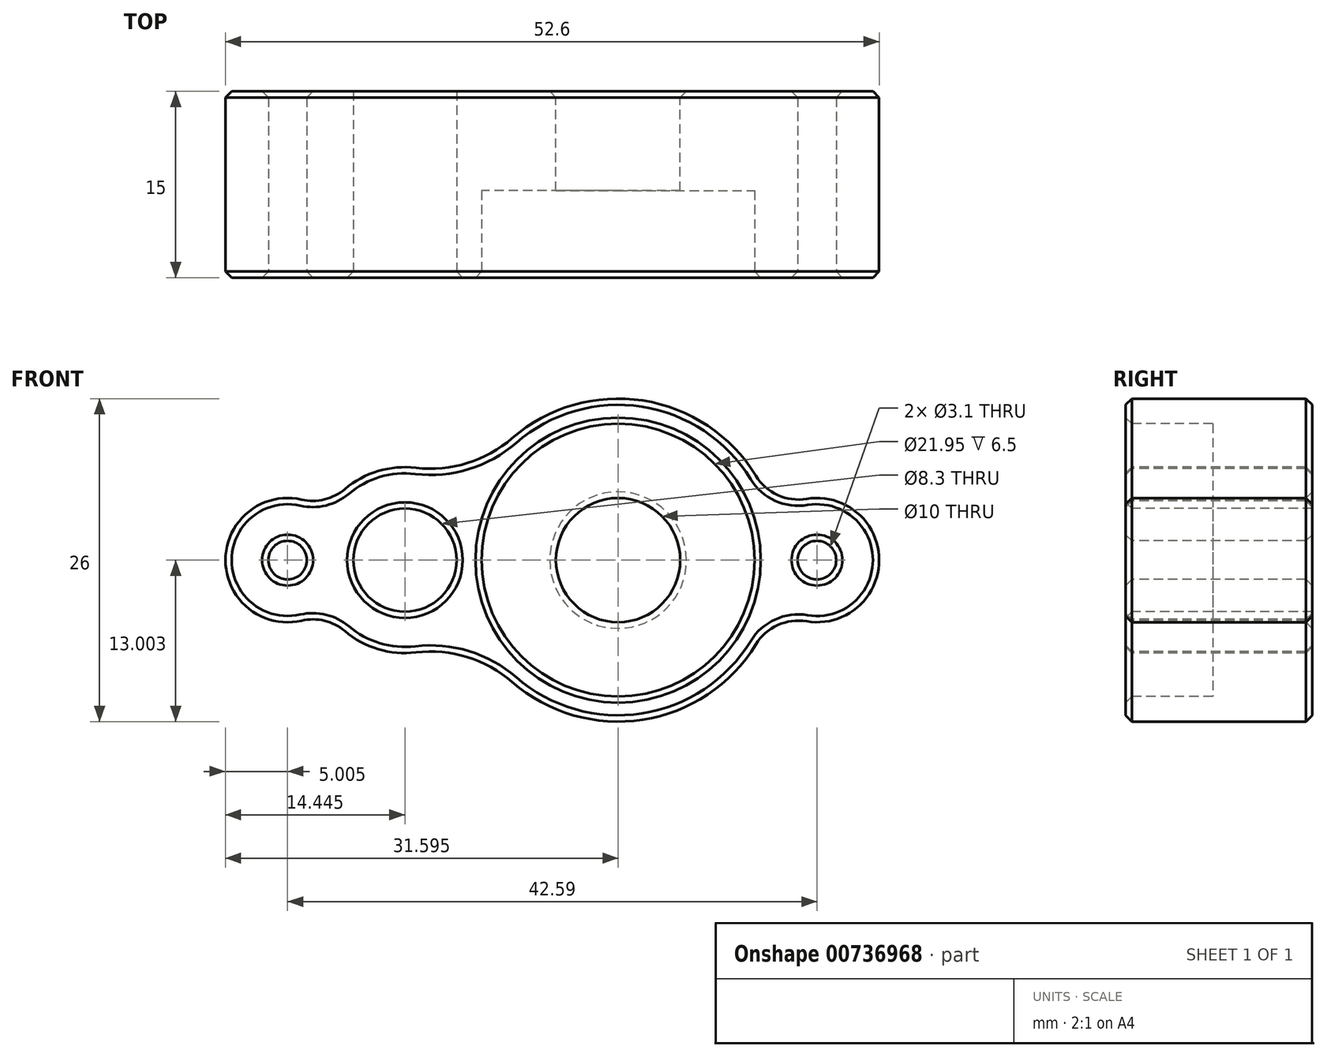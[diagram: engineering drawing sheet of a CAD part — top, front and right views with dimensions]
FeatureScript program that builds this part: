
annotation { "Feature Type Name" : "Feature", "Feature Type Description" : "" }
export const myFeature = defineFeature(function(context is Context, id is Id, definition is map)
    precondition{}
    {
        {
            var Q0;
            Q0=qCreatedBy(makeId("Front.planeOp"),FACE);
            cPlane(context, id + "F0", {"entities" : qUnion([Q0]), "cplaneType" : CPlaneType.OFFSET, "offset" : 7.5 * mm, "width" : 150 * mm, "height" : 150 * mm});
        }
        {
            var Q0;
            Q0=qCreatedBy(id+"F0.planeOp",FACE);
            var sketch = newSketch(context, id + "F1", { "sketchPlane" : qUnion([Q0])});
            skPoint(sketch, "E0.0", {"position": v(-5.85, 0) * mm});
            skPoint(sketch, "E1.0", {"position": v(16.44, 0) * mm});
            skPoint(sketch, "E2.0", {"position": v(-16.04, 0.76) * mm});
            skPoint(sketch, "E3.0", {"position": v(-7.3, 0) * mm});
            skPoint(sketch, "E4.0", {"position": v(19.77, -0.28) * mm});
            skPoint(sketch, "E5.0", {"position": v(22.82, 0.26) * mm});
            skPoint(sketch, "E6.0", {"position": v(-22.82, -0.28) * mm});
            skPoint(sketch, "E7.0", {"position": v(-19.77, 0.26) * mm});
            skPoint(sketch, "E8.0", {"position": v(5.3, 11.14) * mm});
            skPoint(sketch, "E9.0", {"position": v(-11.7, 4.4) * mm});
            skPoint(sketch, "E10.0", {"position": v(-21.03, 1.52) * mm});
            skPoint(sketch, "E11.0", {"position": v(20.3, 1.18) * mm});
            skCircle(sketch, "E12", {"center": v(21.3, 0) * mm, "radius": 1.55 * mm});
            skCircle(sketch, "E13", {"center": v(-21.3, 0) * mm, "radius": 1.55 * mm});
            skPoint(sketch, "E14.0", {"position": v(-22.16, 4.92) * mm});
            skArc(sketch, "E15", {"start": v(-20.17, 4.86) * mm, "mid": v(-26.3, 0) * mm, "end": v(-20.17, -4.88) * mm});
            skPoint(sketch, "E16.0", {"position": v(-12.48, 7.45) * mm});
            skPoint(sketch, "E17.0", {"position": v(4.86, 12.99) * mm});
            skPoint(sketch, "E18.0", {"position": v(22.16, 4.92) * mm});
            skArc(sketch, "E19", {"start": v(-10.97, 7.43) * mm, "mid": v(-14, 7.16) * mm, "end": v(-16.69, 5.7) * mm});
            skArc(sketch, "E20", {"start": v(-3.23, -9.82) * mm, "mid": v(7.28, -12.86) * mm, "end": v(16.38, -6.8) * mm});
            skArc(sketch, "E21.trimOffspring", {"start": v(-16.69, -5.72) * mm, "mid": v(-14, -7.18) * mm, "end": v(-10.97, -7.44) * mm});
            skArc(sketch, "E22.trimOffspring", {"start": v(16.38, 6.78) * mm, "mid": v(7.28, 12.84) * mm, "end": v(-3.23, 9.8) * mm});
            skArc(sketch, "E23.trimOffspring", {"start": v(20.46, -4.94) * mm, "mid": v(26.3, 0) * mm, "end": v(20.46, 4.92) * mm});
            skCircle(sketch, "E24", {"center": v(5.3, 0) * mm, "radius": 10.97 * mm});
            skCircle(sketch, "E25", {"center": v(21.3, 0) * mm, "radius": 1.25 * mm});
            skCircle(sketch, "E26", {"center": v(-21.3, 0) * mm, "radius": 1.25 * mm});
            skPoint(sketch, "E27.visualSharp", {"position": v(-18.22, 3.93) * mm});
            skArc(sketch, "E27.filletArc", {"start": v(-20.17, 4.86) * mm, "mid": v(-18.33, 4.87) * mm, "end": v(-16.69, 5.7) * mm});
            skPoint(sketch, "E28.visualSharp", {"position": v(-18.22, -3.95) * mm});
            skArc(sketch, "E28.filletArc", {"start": v(-16.69, -5.72) * mm, "mid": v(-18.33, -4.89) * mm, "end": v(-20.17, -4.88) * mm});
            skPoint(sketch, "E29.visualSharp", {"position": v(-6.57, 5.3) * mm});
            skArc(sketch, "E29.filletArc", {"start": v(-10.97, 7.43) * mm, "mid": v(-6.85, 7.8) * mm, "end": v(-3.23, 9.8) * mm});
            skPoint(sketch, "E30.visualSharp", {"position": v(-6.57, -5.31) * mm});
            skArc(sketch, "E30.filletArc", {"start": v(-3.23, -9.82) * mm, "mid": v(-6.85, -7.81) * mm, "end": v(-10.97, -7.44) * mm});
            skPoint(sketch, "E31.visualSharp", {"position": v(17.8, -3.58) * mm});
            skArc(sketch, "E31.filletArc", {"start": v(20.46, -4.94) * mm, "mid": v(18.14, -5.24) * mm, "end": v(16.38, -6.8) * mm});
            skPoint(sketch, "E32.visualSharp", {"position": v(17.8, 3.56) * mm});
            skArc(sketch, "E32.filletArc", {"start": v(16.38, 6.78) * mm, "mid": v(18.14, 5.23) * mm, "end": v(20.46, 4.92) * mm});
            skCircle(sketch, "E33", {"center": v(-11.85, 0) * mm, "radius": 4.15 * mm});
            skSolve(sketch);
        }
        {
            var Q0;
            Q0=makeQuery(id+"F1.imprint","IMPRINT",FACE,{"disambiguationData":[TD([[makeQuery(id+"F1.imprint","IMPRINT",EDGE,{"derivedFrom":sQuery(id+"F1.wireOp",EDGE,"ee63c072-4f0e-46bd-9d90-5885ff48c119")}),-1.0]])]});
            var Q1;
            Q1=makeQuery(id+"F1.imprint","IMPRINT",FACE,{"disambiguationData":[TD([[makeQuery(id+"F1.imprint","IMPRINT",EDGE,{"derivedFrom":sQuery(id+"F1.wireOp",EDGE,"E12")}),-1.0]])]});
            extrude(context, id + "F2", {"entities" : qUnion([Q0, Q1]), "oppositeDirection" : true, "depth" : 15 * mm, "offsetDistance" : 25 * mm});
        }
        {
            var Q0;
            Q0=makeQuery(id+"F2.opExtrude","CAP_FACE",FACE,{"disambiguationData":[OSD([sQuery(id+"F1.wireOp",EDGE,"ee63c072-4f0e-46bd-9d90-5885ff48c119"),sQuery(id+"F1.wireOp",EDGE,"E12"),sQuery(id+"F1.wireOp",EDGE,"E13"),sQuery(id+"F1.wireOp",EDGE,"E15"),sQuery(id+"F1.wireOp",EDGE,"E19"),sQuery(id+"F1.wireOp",EDGE,"E20"),sQuery(id+"F1.wireOp",EDGE,"E21.trimOffspring"),sQuery(id+"F1.wireOp",EDGE,"E22.trimOffspring"),sQuery(id+"F1.wireOp",EDGE,"E23.trimOffspring"),sQuery(id+"F1.wireOp",EDGE,"E24"),sQuery(id+"F1.wireOp",EDGE,"E27.filletArc"),sQuery(id+"F1.wireOp",EDGE,"E28.filletArc"),sQuery(id+"F1.wireOp",EDGE,"E29.filletArc"),sQuery(id+"F1.wireOp",EDGE,"E30.filletArc"),sQuery(id+"F1.wireOp",EDGE,"E31.filletArc"),sQuery(id+"F1.wireOp",EDGE,"E32.filletArc")])],"isStart":false});
            var sketch = newSketch(context, id + "F3", { "sketchPlane" : qUnion([Q0])});
            skCircle(sketch, "E34.0", {"center": v(-5.3, 0) * mm, "radius": 10.97 * mm});
            skCircle(sketch, "E35", {"center": v(-5.3, 0) * mm, "radius": 5 * mm});
            skSolve(sketch);
        }
        {
            var Q0;
            Q0=makeQuery(id+"F3.imprint","IMPRINT",FACE,{"disambiguationData":[TD([[makeQuery(id+"F3.imprint","IMPRINT",EDGE,{"derivedFrom":sQuery(id+"F3.wireOp",EDGE,"E34.0")}),-1.0]])]});
            extrude(context, id + "F4", {"entities" : qUnion([Q0]), "operationType" : NewBodyOperationType.ADD, "oppositeDirection" : true, "depth" : 8 * mm, "offsetDistance" : 25 * mm});
        }
        {
            var Q0;
            Q0=makeQuery(id+"F2.opExtrude","CAP_EDGE",EDGE,{"disambiguationData":[OSD([sQuery(id+"F1.wireOp",EDGE,"E29.filletArc")])],"isStart":true});
            var Q1;
            Q1=makeQuery(id+"F2.opExtrude","CAP_EDGE",EDGE,{"disambiguationData":[OSD([sQuery(id+"F1.wireOp",EDGE,"E22.trimOffspring")])],"isStart":true});
            var Q2;
            Q2=makeQuery(id+"F2.opExtrude","CAP_EDGE",EDGE,{"disambiguationData":[OSD([sQuery(id+"F1.wireOp",EDGE,"E32.filletArc")])],"isStart":true});
            var Q3;
            Q3=makeQuery(id+"F2.opExtrude","CAP_EDGE",EDGE,{"disambiguationData":[OSD([sQuery(id+"F1.wireOp",EDGE,"E23.trimOffspring")])],"isStart":true});
            var Q4;
            Q4=makeQuery(id+"F2.opExtrude","CAP_EDGE",EDGE,{"disambiguationData":[OSD([sQuery(id+"F1.wireOp",EDGE,"E31.filletArc")])],"isStart":true});
            var Q5;
            Q5=makeQuery(id+"F2.opExtrude","CAP_EDGE",EDGE,{"disambiguationData":[OSD([sQuery(id+"F1.wireOp",EDGE,"E20")])],"isStart":true});
            var Q6;
            Q6=makeQuery(id+"F2.opExtrude","CAP_EDGE",EDGE,{"disambiguationData":[OSD([sQuery(id+"F1.wireOp",EDGE,"E30.filletArc")])],"isStart":true});
            var Q7;
            Q7=makeQuery(id+"F2.opExtrude","CAP_EDGE",EDGE,{"disambiguationData":[OSD([sQuery(id+"F1.wireOp",EDGE,"E21.trimOffspring")])],"isStart":true});
            var Q8;
            Q8=makeQuery(id+"F2.opExtrude","CAP_EDGE",EDGE,{"disambiguationData":[OSD([sQuery(id+"F1.wireOp",EDGE,"E28.filletArc")])],"isStart":true});
            var Q9;
            Q9=makeQuery(id+"F2.opExtrude","CAP_EDGE",EDGE,{"disambiguationData":[OSD([sQuery(id+"F1.wireOp",EDGE,"E15")])],"isStart":true});
            var Q10;
            Q10=makeQuery(id+"F2.opExtrude","CAP_EDGE",EDGE,{"disambiguationData":[OSD([sQuery(id+"F1.wireOp",EDGE,"E27.filletArc")])],"isStart":true});
            var Q11;
            Q11=makeQuery(id+"F2.opExtrude","CAP_EDGE",EDGE,{"disambiguationData":[OSD([sQuery(id+"F1.wireOp",EDGE,"E19")])],"isStart":true});
            var Q12;
            Q12=makeQuery(id+"F2.opExtrude","CAP_EDGE",EDGE,{"disambiguationData":[OSD([sQuery(id+"F1.wireOp",EDGE,"E24")])],"isStart":true});
            var Q13;
            Q13=makeQuery(id+"F2.opExtrude","CAP_EDGE",EDGE,{"disambiguationData":[OSD([sQuery(id+"F1.wireOp",EDGE,"ee63c072-4f0e-46bd-9d90-5885ff48c119")])],"isStart":true});
            var Q14;
            Q14=makeQuery(id+"F2.opExtrude","CAP_EDGE",EDGE,{"disambiguationData":[OSD([sQuery(id+"F1.wireOp",EDGE,"E13")])],"isStart":true});
            var Q15;
            Q15=makeQuery(id+"F2.opExtrude","CAP_EDGE",EDGE,{"disambiguationData":[OSD([sQuery(id+"F1.wireOp",EDGE,"E12")])],"isStart":true});
            var Q16;
            Q16=makeQuery(id+"F2.opExtrude","CAP_EDGE",EDGE,{"disambiguationData":[OSD([sQuery(id+"F1.wireOp",EDGE,"E22.trimOffspring")])],"isStart":false});
            var Q17;
            Q17=makeQuery(id+"F2.opExtrude","CAP_EDGE",EDGE,{"disambiguationData":[OSD([sQuery(id+"F1.wireOp",EDGE,"ee63c072-4f0e-46bd-9d90-5885ff48c119")])],"isStart":false});
            var Q18;
            Q18=makeQuery(id+"F2.opExtrude","CAP_EDGE",EDGE,{"disambiguationData":[OSD([sQuery(id+"F1.wireOp",EDGE,"E13")])],"isStart":false});
            var Q19;
            Q19=makeQuery(id+"F4.opExtrude","CAP_EDGE",EDGE,{"disambiguationData":[OSD([sQuery(id+"F3.wireOp",EDGE,"E35")])],"isStart":true});
            var Q20;
            Q20=makeQuery(id+"F2.opExtrude","CAP_EDGE",EDGE,{"disambiguationData":[OSD([sQuery(id+"F1.wireOp",EDGE,"E12")])],"isStart":false});
            var Q21;
            Q21=makeQuery(id+"F2.opExtrude","CAP_EDGE",EDGE,{"disambiguationData":[OSD([sQuery(id+"F1.wireOp",EDGE,"E33")])],"isStart":true});
            chamfer(context, id + "F5", {"entities" : qUnion([Q0, Q1, Q2, Q3, Q4, Q5, Q6, Q7, Q8, Q9, Q10, Q11, Q12, Q13, Q14, Q15, Q16, Q17, Q18, Q19, Q20, Q21]), "width" : .5 * mm, "tangentPropagation" : true});
        }
    });
